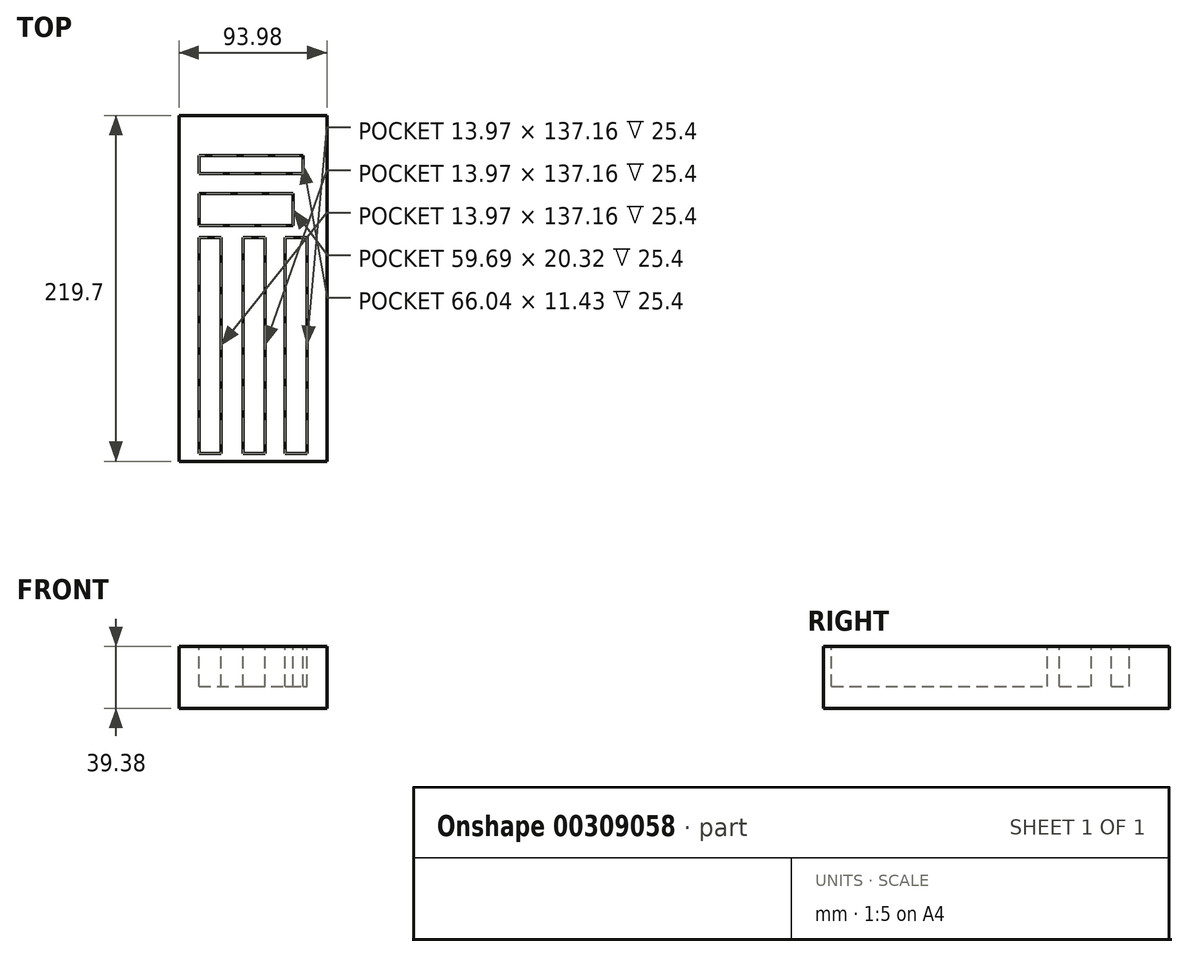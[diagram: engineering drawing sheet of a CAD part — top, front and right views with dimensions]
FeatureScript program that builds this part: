
annotation { "Feature Type Name" : "Feature", "Feature Type Description" : "" }
export const myFeature = defineFeature(function(context is Context, id is Id, definition is map)
    precondition{}
    {
        {
            var Q0;
            Q0=qCreatedBy(makeId("Top.planeOp"),FACE);
            var sketch = newSketch(context, id + "F0", { "sketchPlane" : qUnion([Q0])});
            skLineSegment(sketch, "E0.bottom", {"start": v(-46.99, 109.86) * mm, "end": v(47, 109.86) * mm});
            skLineSegment(sketch, "E0.top", {"start": v(-47, -109.86) * mm, "end": v(46.99, -109.86) * mm});
            skLineSegment(sketch, "E0.left", {"start": v(-46.99, 109.86) * mm, "end": v(-47, -109.86) * mm});
            skLineSegment(sketch, "E0.right", {"start": v(47, 109.85) * mm, "end": v(46.99, -109.86) * mm});
            skPoint(sketch, "E0.middle", {"position": v(0, 0) * mm});
            skSolve(sketch);
        }
        {
            var Q0;
            Q0=makeQuery(id+"F0.imprint","IMPRINT",FACE,{"disambiguationData":[TD([[makeQuery(id+"F0.imprint","IMPRINT",EDGE,{"derivedFrom":sQuery(id+"F0.wireOp",EDGE,"E0.bottom")}),-1.0]])]});
            extrude(context, id + "F1", {"entities" : qUnion([Q0]), "depth" : 19.68 * mm});
        }
        {
            var Q0;
            Q0=makeQuery(id+"F1.opExtrude","CAP_FACE",FACE,{"disambiguationData":[OSD([sQuery(id+"F0.wireOp",EDGE,"E0.bottom"),sQuery(id+"F0.wireOp",EDGE,"E0.top"),sQuery(id+"F0.wireOp",EDGE,"E0.left"),sQuery(id+"F0.wireOp",EDGE,"E0.right")])],"isStart":true});
            extrude(context, id + "F2", {"entities" : qUnion([Q0]), "operationType" : NewBodyOperationType.ADD, "depth" : 19.68 * mm});
        }
        {
            var Q0;
            Q0=makeQuery(id+"F1.opExtrude","CAP_FACE",FACE,{"disambiguationData":[OSD([sQuery(id+"F0.wireOp",EDGE,"E0.bottom"),sQuery(id+"F0.wireOp",EDGE,"E0.top"),sQuery(id+"F0.wireOp",EDGE,"E0.left"),sQuery(id+"F0.wireOp",EDGE,"E0.right")])],"isStart":false});
            var sketch = newSketch(context, id + "F3", { "sketchPlane" : qUnion([Q0])});
            skLineSegment(sketch, "E1", {"start": v(-47, -109.86) * mm, "end": v(-34.3, -109.86) * mm});
            skLineSegment(sketch, "E2", {"start": v(-34.3, -109.86) * mm, "end": v(-34.3, -97.16) * mm});
            skLineSegment(sketch, "E3", {"start": v(46.99, -109.86) * mm, "end": v(34.29, -109.86) * mm});
            skLineSegment(sketch, "E4", {"start": v(34.29, -109.86) * mm, "end": v(34.29, -97.16) * mm});
            skLineSegment(sketch, "E5.bottom", {"start": v(34.29, -109.86) * mm, "end": v(20.32, -109.86) * mm});
            skLineSegment(sketch, "E5.top", {"start": v(34.29, 27.3) * mm, "end": v(20.32, 27.3) * mm});
            skLineSegment(sketch, "E5.left", {"start": v(34.29, -109.86) * mm, "end": v(34.29, 27.3) * mm});
            skLineSegment(sketch, "E5.right", {"start": v(20.32, -109.86) * mm, "end": v(20.32, 27.3) * mm});
            skLineSegment(sketch, "E6.bottom", {"start": v(-34.3, -109.86) * mm, "end": v(-20.32, -109.86) * mm});
            skLineSegment(sketch, "E6.top", {"start": v(-34.3, 27.3) * mm, "end": v(-20.32, 27.3) * mm});
            skLineSegment(sketch, "E6.left", {"start": v(-34.3, -109.86) * mm, "end": v(-34.3, 27.3) * mm});
            skLineSegment(sketch, "E6.right", {"start": v(-20.32, -109.86) * mm, "end": v(-20.32, 27.3) * mm});
            skLineSegment(sketch, "E7", {"start": v(-20.32, -109.86) * mm, "end": v(-7.62, -109.86) * mm});
            skLineSegment(sketch, "E8", {"start": v(20.32, -109.86) * mm, "end": v(7.62, -109.86) * mm});
            skLineSegment(sketch, "E9.bottom", {"start": v(7.62, -109.86) * mm, "end": v(-6.35, -109.86) * mm});
            skLineSegment(sketch, "E9.top", {"start": v(7.62, 27.3) * mm, "end": v(-6.35, 27.3) * mm});
            skLineSegment(sketch, "E9.left", {"start": v(7.62, -109.86) * mm, "end": v(7.62, 27.3) * mm});
            skLineSegment(sketch, "E9.right", {"start": v(-6.35, -109.86) * mm, "end": v(-6.35, 27.3) * mm});
            skLineSegment(sketch, "E10", {"start": v(-34.3, 40) * mm, "end": v(25.4, 40) * mm});
            skLineSegment(sketch, "E11.top", {"start": v(-34.3, 60.33) * mm, "end": v(25.4, 60.33) * mm});
            skLineSegment(sketch, "E11.left", {"start": v(-34.3, 40) * mm, "end": v(-34.3, 60.33) * mm});
            skLineSegment(sketch, "E11.right", {"start": v(25.4, 40) * mm, "end": v(25.4, 60.33) * mm});
            skLineSegment(sketch, "E12", {"start": v(-34.3, 73.03) * mm, "end": v(-34.3, 84.46) * mm});
            skLineSegment(sketch, "E13", {"start": v(-34.3, 73.03) * mm, "end": v(31.75, 73.03) * mm});
            skLineSegment(sketch, "E14", {"start": v(31.75, 73.03) * mm, "end": v(31.75, 84.46) * mm});
            skLineSegment(sketch, "E15", {"start": v(31.75, 84.46) * mm, "end": v(-34.3, 84.46) * mm});
            skSolve(sketch);
        }
        {
            var Q0;
            Q0 = qSketchRegion(id + "F3", true);
            extrude(context, id + "F4", {"entities" : qUnion([Q0]), "operationType" : NewBodyOperationType.REMOVE, "oppositeDirection" : true, "depth" : 25.4 * mm});
        }
        {
            var Q0;
            Q0=makeQuery(id+"F3.imprint","IMPRINT",FACE,{"disambiguationData":[TD([[makeQuery(id+"F3.imprint","IMPRINT",EDGE,{"derivedFrom":sQuery(id+"F3.wireOp",EDGE,"E10")}),1.0]])]});
            extrude(context, id + "F5", {"entities" : qUnion([Q0]), "operationType" : NewBodyOperationType.REMOVE, "oppositeDirection" : true, "depth" : 6.35 * mm});
        }
        {
            var Q0;
            Q0=makeQuery(id+"F1.opExtrude","CAP_FACE",FACE,{"disambiguationData":[OSD([sQuery(id+"F0.wireOp",EDGE,"E0.bottom"),sQuery(id+"F0.wireOp",EDGE,"E0.top"),sQuery(id+"F0.wireOp",EDGE,"E0.left"),sQuery(id+"F0.wireOp",EDGE,"E0.right")])],"isStart":false});
            var sketch = newSketch(context, id + "F6", { "sketchPlane" : qUnion([Q0])});
            skLineSegment(sketch, "E16.bottom", {"start": v(-34.3, -109.86) * mm, "end": v(-20.32, -109.86) * mm});
            skLineSegment(sketch, "E16.top", {"start": v(-34.3, 27.3) * mm, "end": v(-20.32, 27.3) * mm});
            skLineSegment(sketch, "E16.left", {"start": v(-34.3, -109.86) * mm, "end": v(-34.3, 27.3) * mm});
            skLineSegment(sketch, "E16.right", {"start": v(-20.32, -109.86) * mm, "end": v(-20.32, 27.3) * mm});
            skLineSegment(sketch, "E17.bottom", {"start": v(-6.35, -109.86) * mm, "end": v(7.62, -109.86) * mm});
            skLineSegment(sketch, "E17.top", {"start": v(-6.35, 27.3) * mm, "end": v(7.62, 27.3) * mm});
            skLineSegment(sketch, "E17.left", {"start": v(-6.35, -109.86) * mm, "end": v(-6.35, 27.3) * mm});
            skLineSegment(sketch, "E17.right", {"start": v(7.62, -109.86) * mm, "end": v(7.62, 27.3) * mm});
            skLineSegment(sketch, "E18.bottom", {"start": v(20.32, -109.86) * mm, "end": v(34.29, -109.86) * mm});
            skLineSegment(sketch, "E18.top", {"start": v(20.32, 27.3) * mm, "end": v(34.29, 27.3) * mm});
            skLineSegment(sketch, "E18.left", {"start": v(20.32, -109.86) * mm, "end": v(20.32, 27.3) * mm});
            skLineSegment(sketch, "E18.right", {"start": v(34.29, -109.86) * mm, "end": v(34.29, 27.3) * mm});
            skSolve(sketch);
        }
        {
            var Q0;
            Q0 = qSketchRegion(id + "F6", true);
            extrude(context, id + "F7", {"entities" : qUnion([Q0]), "operationType" : NewBodyOperationType.ADD, "oppositeDirection" : true, "depth" : 7.62 * mm});
        }
        {
            var Q0;
            {var subQ3=sQuery(id+"F3.wireOp",EDGE,"E5.bottom");Q0=makeQuery(id+"F3.imprint","IMPRINT",FACE,{"disambiguationData":[TD([[makeQuery(id+"F3.imprint","IMPRINT",EDGE,{"derivedFrom":subQ3}),1.0]])]});}
            var Q1;
            Q1=makeQuery(id+"F3.imprint","IMPRINT",FACE,{"disambiguationData":[TD([[makeQuery(id+"F3.imprint","IMPRINT",EDGE,{"derivedFrom":sQuery(id+"F3.wireOp",EDGE,"E9.bottom")}),1.0]])]});
            var Q2;
            {var subQ3=sQuery(id+"F3.wireOp",EDGE,"E6.bottom");Q2=makeQuery(id+"F3.imprint","IMPRINT",FACE,{"disambiguationData":[TD([[makeQuery(id+"F3.imprint","IMPRINT",EDGE,{"derivedFrom":subQ3}),1.0]])]});}
            extrude(context, id + "F8", {"entities" : qUnion([Q0, Q1, Q2]), "operationType" : NewBodyOperationType.REMOVE, "oppositeDirection" : true, "depth" : 12.7 * mm});
        }
        {
            var Q0;
            {var subQ0=sQuery(id+"F0.wireOp",EDGE,"E0.top");Q0=makeQuery(id+"F7.boolean.opBoolean","MERGE",FACE,{"derivedFrom":[makeQuery(id+"F2.boolean.opBoolean","MERGE",FACE,{"derivedFrom":[makeQuery(id+"F1.opExtrude","SWEPT_FACE",FACE,{"disambiguationData":[OSD([subQ0])]}),makeQuery(id+"F2.opExtrude","SWEPT_FACE",FACE,{"disambiguationData":[OSD([subQ0])]})]}),makeQuery(id+"F7.opExtrude","SWEPT_FACE",FACE,{"disambiguationData":[OSD([sQuery(id+"F6.wireOp",EDGE,"E16.bottom")])]}),makeQuery(id+"F7.opExtrude","SWEPT_FACE",FACE,{"disambiguationData":[OSD([sQuery(id+"F6.wireOp",EDGE,"E17.bottom")])]}),makeQuery(id+"F7.opExtrude","SWEPT_FACE",FACE,{"disambiguationData":[OSD([sQuery(id+"F6.wireOp",EDGE,"E18.bottom")])]})]});}
            var sketch = newSketch(context, id + "F9", { "sketchPlane" : qUnion([Q0])});
            skLineSegment(sketch, "E19.bottom", {"start": v(-34.3, 19.69) * mm, "end": v(-20.32, 19.69) * mm});
            skLineSegment(sketch, "E19.top", {"start": v(-34.3, -5.72) * mm, "end": v(-20.32, -5.72) * mm});
            skLineSegment(sketch, "E19.left", {"start": v(-34.3, 19.69) * mm, "end": v(-34.3, -5.72) * mm});
            skLineSegment(sketch, "E19.right", {"start": v(-20.32, 19.69) * mm, "end": v(-20.32, -5.72) * mm});
            skLineSegment(sketch, "E20.bottom", {"start": v(-6.35, 19.69) * mm, "end": v(7.62, 19.69) * mm});
            skLineSegment(sketch, "E20.top", {"start": v(-6.35, -5.72) * mm, "end": v(7.62, -5.72) * mm});
            skLineSegment(sketch, "E20.left", {"start": v(-6.35, 19.69) * mm, "end": v(-6.35, -5.72) * mm});
            skLineSegment(sketch, "E20.right", {"start": v(7.62, 19.69) * mm, "end": v(7.62, -5.72) * mm});
            skLineSegment(sketch, "E21.bottom", {"start": v(20.32, 19.69) * mm, "end": v(34.29, 19.69) * mm});
            skLineSegment(sketch, "E21.top", {"start": v(20.32, -5.72) * mm, "end": v(34.29, -5.72) * mm});
            skLineSegment(sketch, "E21.left", {"start": v(20.32, 19.69) * mm, "end": v(20.32, -5.72) * mm});
            skLineSegment(sketch, "E21.right", {"start": v(34.29, 19.69) * mm, "end": v(34.29, -5.72) * mm});
            skSolve(sketch);
        }
        {
            var Q0;
            Q0=makeQuery(id+"F9.imprint","IMPRINT",FACE,{"disambiguationData":[TD([[makeQuery(id+"F9.imprint","IMPRINT",EDGE,{"derivedFrom":sQuery(id+"F9.wireOp",EDGE,"E19.bottom")}),-1.0]])]});
            var Q1;
            Q1=makeQuery(id+"F9.imprint","IMPRINT",FACE,{"disambiguationData":[TD([[makeQuery(id+"F9.imprint","IMPRINT",EDGE,{"derivedFrom":sQuery(id+"F9.wireOp",EDGE,"E20.bottom")}),-1.0]])]});
            var Q2;
            Q2=makeQuery(id+"F9.imprint","IMPRINT",FACE,{"disambiguationData":[TD([[makeQuery(id+"F9.imprint","IMPRINT",EDGE,{"derivedFrom":sQuery(id+"F9.wireOp",EDGE,"E21.bottom")}),-1.0]])]});
            extrude(context, id + "F10", {"entities" : qUnion([Q0, Q1, Q2]), "operationType" : NewBodyOperationType.ADD, "oppositeDirection" : true, "depth" : 5.08 * mm});
        }
        {
            var Q0;
            {var subQ0=sQuery(id+"F3.wireOp",EDGE,"E6.top");Q0=makeQuery(id+"F8.boolean.opBoolean","MERGE",FACE,{"derivedFrom":[makeQuery(id+"F4.boolean.opBoolean","COPY",FACE,{"derivedFrom":makeQuery(id+"F4.opExtrude","SWEPT_FACE",FACE,{"disambiguationData":[OSD([subQ0])]})}),makeQuery(id+"F8.opExtrude","SWEPT_FACE",FACE,{"disambiguationData":[OSD([subQ0])]})]});}
            var Q1;
            {var subQ0=sQuery(id+"F3.wireOp",EDGE,"E9.top");Q1=makeQuery(id+"F8.boolean.opBoolean","MERGE",FACE,{"derivedFrom":[makeQuery(id+"F4.boolean.opBoolean","COPY",FACE,{"derivedFrom":makeQuery(id+"F4.opExtrude","SWEPT_FACE",FACE,{"disambiguationData":[OSD([subQ0])]})}),makeQuery(id+"F8.opExtrude","SWEPT_FACE",FACE,{"disambiguationData":[OSD([subQ0])]})]});}
            var Q2;
            {var subQ0=sQuery(id+"F3.wireOp",EDGE,"E5.top");Q2=makeQuery(id+"F8.boolean.opBoolean","MERGE",FACE,{"derivedFrom":[makeQuery(id+"F4.boolean.opBoolean","COPY",FACE,{"derivedFrom":makeQuery(id+"F4.opExtrude","SWEPT_FACE",FACE,{"disambiguationData":[OSD([subQ0])]})}),makeQuery(id+"F8.opExtrude","SWEPT_FACE",FACE,{"disambiguationData":[OSD([subQ0])]})]});}
            extrude(context, id + "F11", {"entities" : qUnion([Q0, Q1, Q2]), "operationType" : NewBodyOperationType.REMOVE, "oppositeDirection" : true, "depth" : 5.08 * mm});
        }
    });
